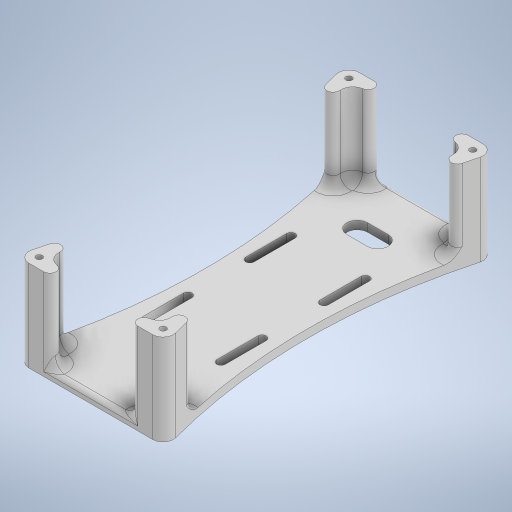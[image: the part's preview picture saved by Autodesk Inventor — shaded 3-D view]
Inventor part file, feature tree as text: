
AUTODESK INVENTOR PART (.ipt)
format: ipt  version: 2023 (Build 270158000, 158)  size: 630,784 bytes
history: native  units: mm
features: sketch x5, extrude x4, mirror x4, fillet x2, hole x1, projected_geometry x1
ambient origin geometry x8: Origin, YZ Plane, XZ Plane, XY Plane, X Axis, Y Axis, Z Axis, Center Point
bodies: Solid1 (feature_tree)
feature tree (17):
  extrude  "Extrusion1"  Depth=5.0mm
  extrude  "Extrusion2"  Depth=40.0mm TaperAngle=0.0deg
  mirror  "Mirror1"
  mirror  "Mirror2"
  fillet  "Fillet2"  Radius=2.0mm
  hole  "Hole1"  [1 undecoded]
  extrude  "Extrusion3"  Depth=18.0mm
  mirror  "Mirror3"
  mirror  "Mirror4"
  extrude  "Extrusion4"  Depth=5.0mm TaperAngle=0.0deg
  fillet  "Fillet3"  Radius=10.0mm
  sketch  "Sketch1"  dims[d0=160.0mm d3=5.0mm]
  sketch  "Sketch2"  dims[d5=4.0mm d6=0.0mm d7=40.0mm d8=0.0mm d10=2.0mm]
  sketch  "Sketch4"  dims[d11=3.0mm d12=6.0mm d13=5.5mm d14=2.0mm d15=90.0deg d16=20.0mm d17=20.594885mm d27=4.0mm]
  sketch  "Sketch6"  dims[d28=20.0mm d29=18.0mm]
  sketch  "Sketch7"  dims[d31=25.0mm d32=10.0mm d33=0.0mm d36=10.0mm d37=0.0mm d39=60.0mm d40=50.0mm d47=3.0mm d48=90.0deg d50=5.0mm d51=54.0mm d52=10.0mm d54=20.0mm d9=0.0mm]
  projected_geometry  "Projected Loop1"
note: 1 required parameter value undecoded (feature->parameter linkage not recoverable at this tier; creation-order binding heuristic only, values carry confidence <= 0.55)
